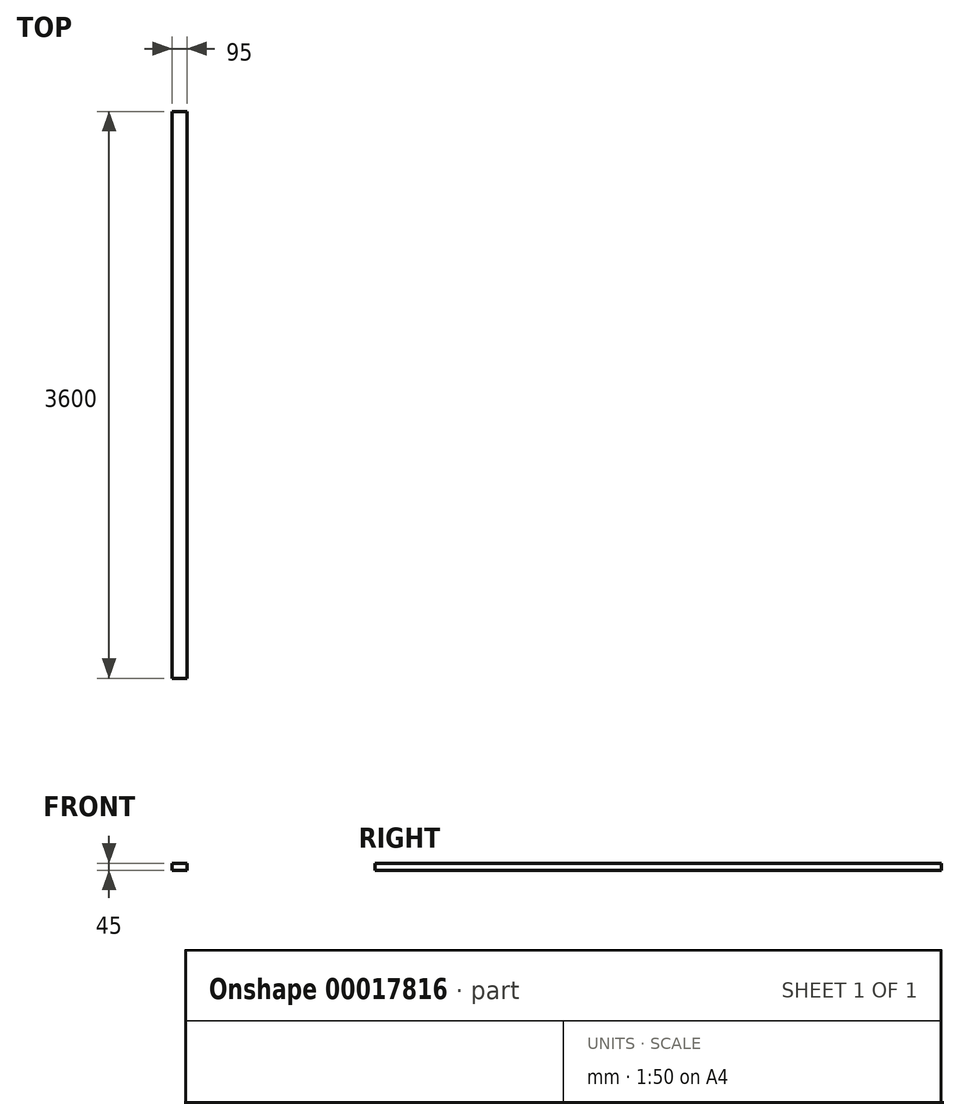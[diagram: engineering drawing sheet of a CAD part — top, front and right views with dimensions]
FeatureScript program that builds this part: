
annotation { "Feature Type Name" : "Feature", "Feature Type Description" : "" }
export const myFeature = defineFeature(function(context is Context, id is Id, definition is map)
    precondition{}
    {
        {
            var Q0;
            Q0=qCreatedBy(makeId("Front.planeOp"),FACE);
            var sketch = newSketch(context, id + "F0", { "sketchPlane" : qUnion([Q0])});
            skLineSegment(sketch, "E0.rect.bottom", {"start": v(-47.5, 22.5) * mm, "end": v(47.5, 22.5) * mm});
            skLineSegment(sketch, "E0.rect.top", {"start": v(-47.5, -22.5) * mm, "end": v(47.5, -22.5) * mm});
            skLineSegment(sketch, "E0.rect.left", {"start": v(-47.5, 22.5) * mm, "end": v(-47.5, -22.5) * mm});
            skLineSegment(sketch, "E0.rect.right", {"start": v(47.5, 22.5) * mm, "end": v(47.5, -22.5) * mm});
            skPoint(sketch, "E0.rect.middle", {"position": v(0, 0) * mm});
            skSolve(sketch);
        }
        {
            var Q0;
            Q0 = qSketchRegion(id + "F0", true);
            extrude(context, id + "F1", {"entities" : qUnion([Q0]), "depth" : 3600 * mm});
        }
    });
